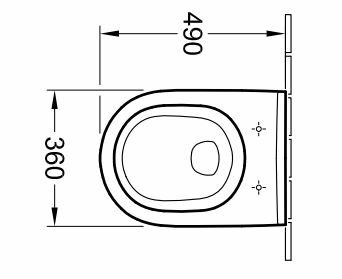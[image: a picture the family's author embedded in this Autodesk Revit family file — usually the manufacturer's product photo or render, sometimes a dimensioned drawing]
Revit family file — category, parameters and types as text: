
# Revit family: Tiefspülklosett spülrandlos 5614R0
name_source: partatom
category: Plumbing Fixtures
revit_build: Autodesk Revit 2016 (Build: 20150714_1515(x64)
units: mm (PartAtom-declared; Revit-internal decimal feet)

## family parameters
Always vertical = Yes
Cut with Voids When Loaded = No
OmniClass Number = 23.45.00.00
OmniClass Title = Sanitary, Laundry, and Cleaning Equipment
Part Type = Normal
Room Calculation Point = No
Round Connector Dimension = Use Diameter
Shared = No
Work Plane-Based = No

## types (1)
- Tiefspülklosett spülrandlos 5614R0
    Manufacturer = Villeroy and Boch
    Model = Tiefspülklosett spülrandlos 5614R0
    URL = https://pro.villeroy-boch.com
    depth = 560 mm  [stored 1.83727 ft]
    height = 415 mm  [stored 1.36155 ft]
    material = ceramic white
    width = 370 mm  [stored 1.21391 ft]

note: [stored X ft] marks values corroborated as IEEE doubles in the binary element streams (Revit-internal decimal feet)

## geometry (parser evidence)
native form markers: Sweep x2
no freeform markers — native parametric forms only
